# Revit family: Faucet-Kitchen-KOHLER-Simplice-K-22036
name_source: partatom
category: Plumbing Fixtures
revit_build: Autodesk Revit 2017 (Build: 20160225_1515(x64)
units: mm (PartAtom-declared; Revit-internal decimal feet)

## family parameters
Cut with Voids When Loaded = No
Host = Face
OmniClass Number = 23.31.11.00
OmniClass Title = Faucets
Part Type = Normal
Room Calculation Point = No
Round Connector Dimension = Use Diameter
Shared = No

## types (3) — shared parameters
ADA Compliant = Yes
Apparent Load = 1440 VA
Assembly Code = D2010
CW Connection = Yes
Cold Water Inlet = Cold Water Inlet
Date Modified = 01/17/2020
Default Elevation = 36"
Description = Touchless pull-down kitchen sink faucet
Drain Included = No
Electrical Connector = Yes
Electrical Note = One dedicated circuit required
Flow Rate = 2 GPM
HW Connection = Yes
Handle Clearance = 3 5/16"
Hot Water Inlet = Hot Water Inlet
Length = 9"
Manufacturer = KOHLER Co.
MasterFormat 1995 = 15410
MasterFormat 2004 = 22.41.39
Material = Premium Metal Construction
Pressure = 60.00 psi
Product Documentation Link = https://www.us.kohler.com
Product Name = Simplice
Product Page URL = http://www.us.kohler.com
Spout Reach = 9"
URL = https://www.us.kohler.com
Vent Connection = No
Voltage = 120 V
Waste Connection = No
Waste Water Outlet = Waste Water Outlet
WaterSense Certified = No

## per-type parameters (varying)
| type | Finish | Model | Type |
| CP - Polished Chrome | Kohler-Metal-CP-Polished_Chrome | K-22036-CP | 1 |
| VS - Vibrant Stainless | Kohler-Metal-VS-Vibrant_Stainless | K-22036-VS | 2 |
| BL - Matte Black | Kohler-Metal-BL-Matte_Black | K-22036-BL | 3 |

## geometry (parser evidence)
native form markers: Sweep x8
no freeform markers — native parametric forms only
